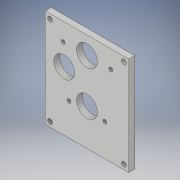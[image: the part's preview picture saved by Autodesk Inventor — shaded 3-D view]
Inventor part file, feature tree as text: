
AUTODESK INVENTOR PART (.ipt)
format: ipt  version: 2018 (Build 220112000, 112)  size: 149,504 bytes
history: native  units: in
note: dims shown in document units (in); Inventor stores cm internally (conversion verified against a paired STEP export)
features: extrude x3, sketch x3
ambient origin geometry x8: Origin, YZ Plane, XZ Plane, XY Plane, X Axis, Y Axis, Z Axis, Center Point
bodies: Solid1 (feature_tree)
feature tree (6):
  extrude  "Extrusion1"  Depth=1.35in
  extrude  "Extrusion2"  Depth=0.875in
  extrude  "Extrusion3"  Depth=0.25in
  sketch  "Sketch1"  dims[d0=0.875in d1=1.35in]
  sketch  "Sketch2"  dims[d2=135.0deg d3=0.875in]
  sketch  "Sketch3"  dims[d7=0.882in d8=0.875in d9=1.0in d10=2.0in d11=0.16in d12=0.75in d13=4.125in d14=1.75in d15=0.25in d16=0.0in d17=1.75in d18=0.2in d19=0.2in d20=0.2031in d21=1.0in d22=0.0in d23=0.75in d24=0.188in d25=0.159in d26=1.0in d27=0.0in]
